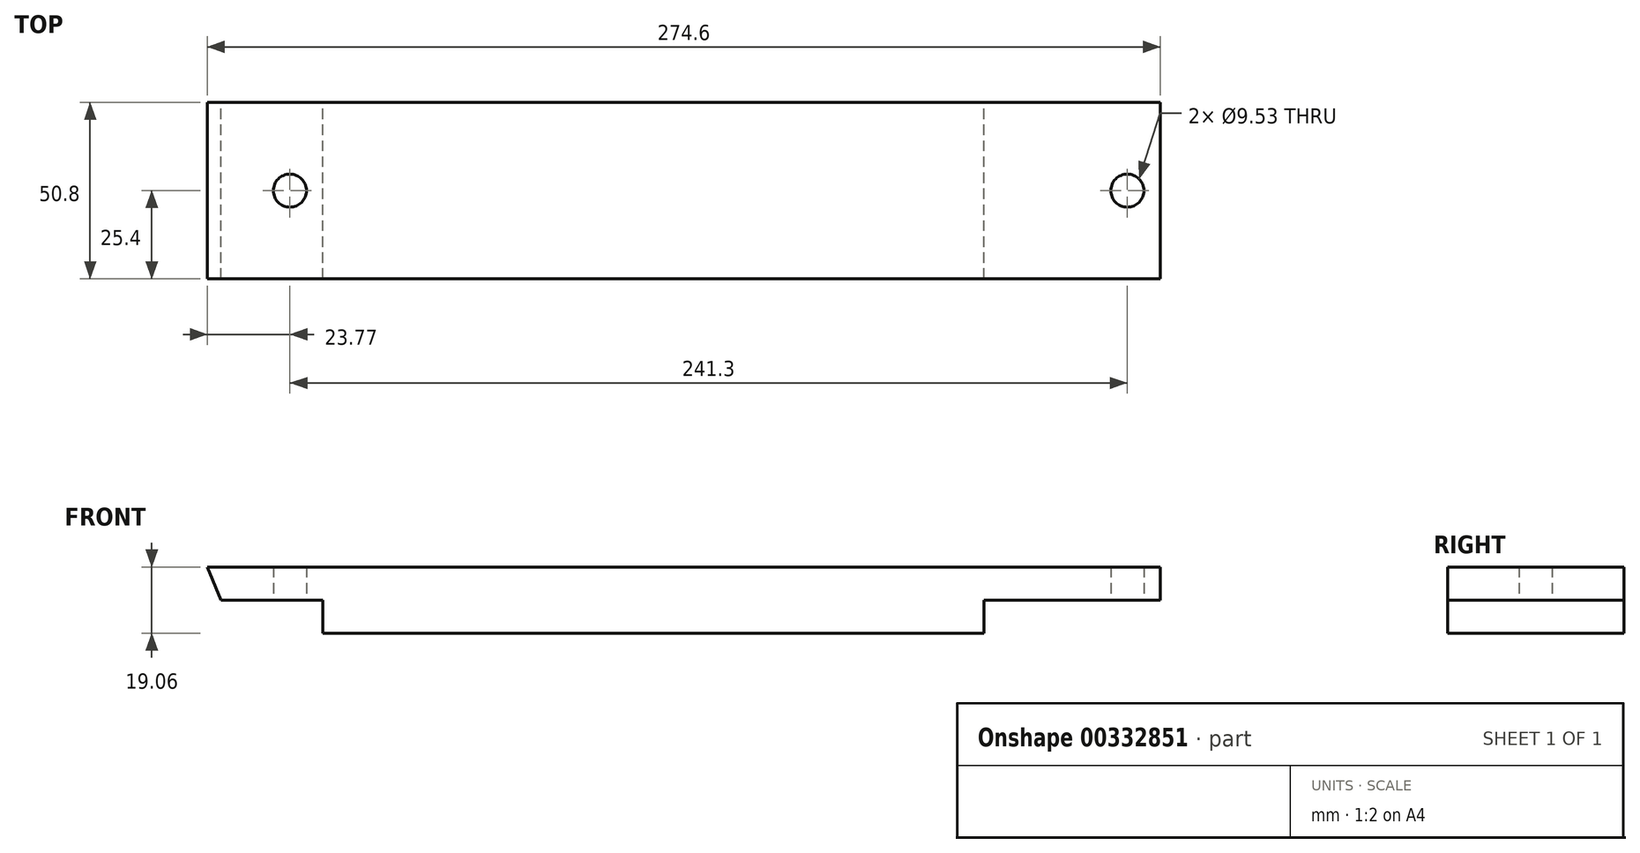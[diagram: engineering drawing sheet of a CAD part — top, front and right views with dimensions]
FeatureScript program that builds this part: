
annotation { "Feature Type Name" : "Feature", "Feature Type Description" : "" }
export const myFeature = defineFeature(function(context is Context, id is Id, definition is map)
    precondition{}
    {
        {
            var Q0;
            Q0=qCreatedBy(makeId("Front.planeOp"),FACE);
            var sketch = newSketch(context, id + "F0", { "sketchPlane" : qUnion([Q0])});
            skLineSegment(sketch, "E0.bottom", {"start": v(29.35, -9.52) * mm, "end": v(219.85, -9.52) * mm});
            skLineSegment(sketch, "E0.right", {"start": v(270.65, 0) * mm, "end": v(270.65, 9.52) * mm});
            skLineSegment(sketch, "E1", {"start": v(0, 0) * mm, "end": v(-3.95, 9.52) * mm});
            skLineSegment(sketch, "E2", {"start": v(270.65, 9.52) * mm, "end": v(-3.95, 9.52) * mm});
            skLineSegment(sketch, "E3.top", {"start": v(0, 0) * mm, "end": v(29.35, 0) * mm});
            skLineSegment(sketch, "E3.right", {"start": v(29.35, -9.52) * mm, "end": v(29.35, 0) * mm});
            skLineSegment(sketch, "E4.top", {"start": v(219.85, 0) * mm, "end": v(270.65, 0) * mm});
            skLineSegment(sketch, "E4.left", {"start": v(219.85, -9.52) * mm, "end": v(219.85, 0) * mm});
            skPoint(sketch, "E4.right.start.orphan", {"position": v(270.65, -9.52) * mm});
            skSolve(sketch);
        }
        {
            var Q0;
            Q0=makeQuery(id+"F0.imprint","IMPRINT",FACE,{"disambiguationData":[TD([[makeQuery(id+"F0.imprint","IMPRINT",EDGE,{"derivedFrom":sQuery(id+"F0.wireOp",EDGE,"E0.bottom")}),1.0]])]});
            extrude(context, id + "F1", {"entities" : qUnion([Q0]), "endBound" : BoundingType.SYMMETRIC, "depth" : 50.8 * mm});
        }
        {
            var Q0;
            Q0=qCreatedBy(makeId("Top.planeOp"),FACE);
            var sketch = newSketch(context, id + "F2", { "sketchPlane" : qUnion([Q0])});
            skCircle(sketch, "E5", {"center": v(261.12, 0) * mm, "radius": 4.76 * mm});
            skCircle(sketch, "E6", {"center": v(19.82, 0) * mm, "radius": 4.76 * mm});
            skSolve(sketch);
        }
        {
            var Q0;
            Q0 = qSketchRegion(id + "F2", true);
            extrude(context, id + "F3", {"entities" : qUnion([Q0]), "operationType" : NewBodyOperationType.REMOVE, "depth" : 25.4 * mm});
        }
    });
